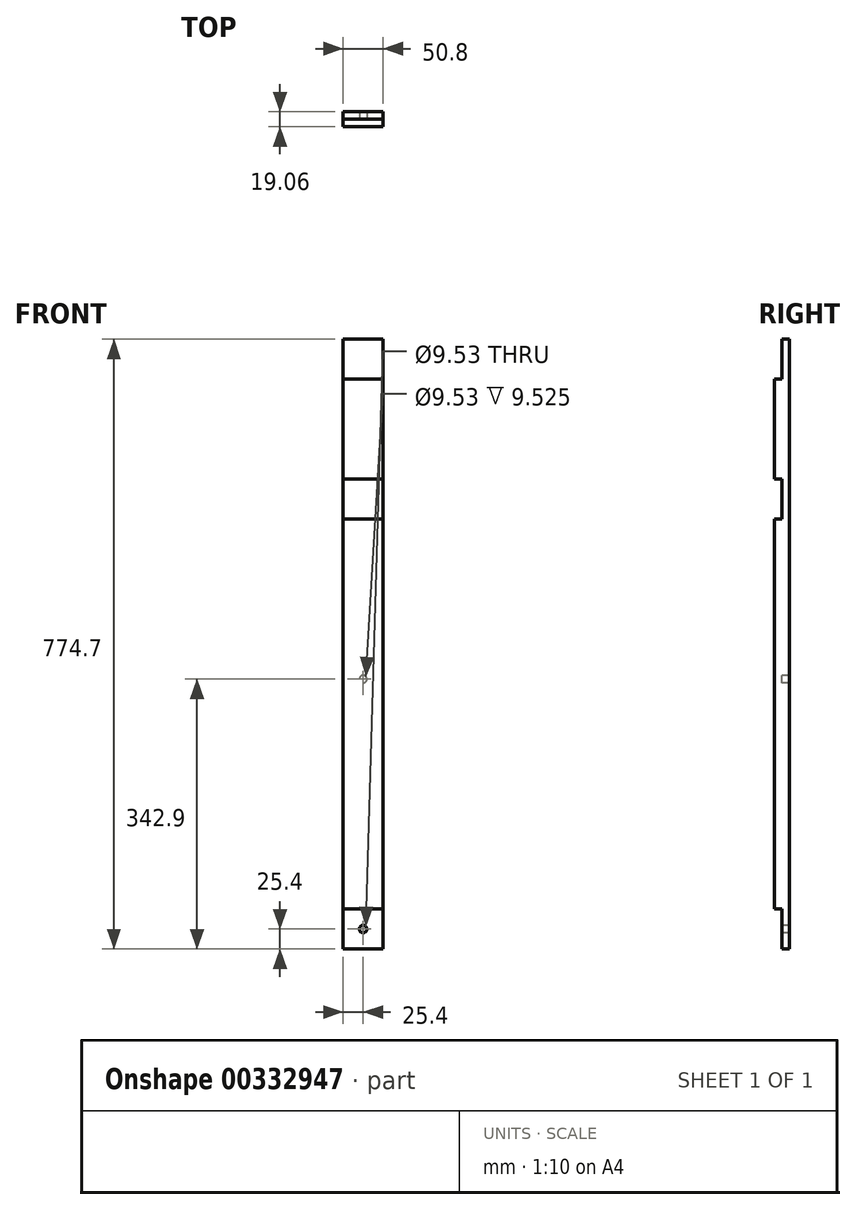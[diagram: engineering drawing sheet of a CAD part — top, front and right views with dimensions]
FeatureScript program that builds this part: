
annotation { "Feature Type Name" : "Feature", "Feature Type Description" : "" }
export const myFeature = defineFeature(function(context is Context, id is Id, definition is map)
    precondition{}
    {
        {
            var Q0;
            Q0=qCreatedBy(makeId("Top.planeOp"),FACE);
            var sketch = newSketch(context, id + "F0", { "sketchPlane" : qUnion([Q0])});
            skLineSegment(sketch, "E0.bottom", {"start": v(25.4, 9.53) * mm, "end": v(-25.4, 9.53) * mm});
            skLineSegment(sketch, "E0.top", {"start": v(25.4, -9.53) * mm, "end": v(-25.4, -9.53) * mm});
            skLineSegment(sketch, "E0.left", {"start": v(25.4, 9.53) * mm, "end": v(25.4, -9.52) * mm});
            skLineSegment(sketch, "E0.right", {"start": v(-25.4, 9.53) * mm, "end": v(-25.4, -9.53) * mm});
            skPoint(sketch, "E0.middle", {"position": v(0, 0) * mm});
            skSolve(sketch);
        }
        {
            var Q0;
            Q0=makeQuery(id+"F0.imprint","IMPRINT",FACE,{"disambiguationData":[TD([[makeQuery(id+"F0.imprint","IMPRINT",EDGE,{"derivedFrom":sQuery(id+"F0.wireOp",EDGE,"E0.bottom")}),1.0]])]});
            var Q1;
            Q1=qSketchRegion(id+"F2",true);
            extrude(context, id + "F1", {"entities" : qUnion([Q0, Q1]), "depth" : 774.7 * mm});
        }
        {
            var Q0;
            Q0=qCreatedBy(makeId("Front.planeOp"),FACE);
            var sketch = newSketch(context, id + "F2", { "sketchPlane" : qUnion([Q0])});
            skLineSegment(sketch, "E1.bottom", {"start": v(-38.77, 0) * mm, "end": v(83.66, 0) * mm});
            skLineSegment(sketch, "E1.top", {"start": v(-38.77, 50.8) * mm, "end": v(83.66, 50.8) * mm});
            skLineSegment(sketch, "E1.left", {"start": v(-38.77, 0) * mm, "end": v(-38.77, 50.8) * mm});
            skLineSegment(sketch, "E1.right", {"start": v(83.66, 0) * mm, "end": v(83.66, 50.8) * mm});
            skLineSegment(sketch, "E2.bottom", {"start": v(-210.36, 723.9) * mm, "end": v(132.8, 723.9) * mm});
            skLineSegment(sketch, "E2.top", {"start": v(-210.36, 774.7) * mm, "end": v(132.8, 774.7) * mm});
            skLineSegment(sketch, "E2.left", {"start": v(-210.36, 723.9) * mm, "end": v(-210.36, 774.7) * mm});
            skLineSegment(sketch, "E2.right", {"start": v(132.8, 723.9) * mm, "end": v(132.8, 774.7) * mm});
            skLineSegment(sketch, "E3.bottom", {"start": v(-168.15, 596.9) * mm, "end": v(92.9, 596.9) * mm});
            skLineSegment(sketch, "E3.top", {"start": v(-168.15, 546.1) * mm, "end": v(92.9, 546.1) * mm});
            skLineSegment(sketch, "E3.left", {"start": v(-168.15, 596.9) * mm, "end": v(-168.15, 546.1) * mm});
            skLineSegment(sketch, "E3.right", {"start": v(92.9, 596.9) * mm, "end": v(92.9, 546.1) * mm});
            skSolve(sketch);
        }
        {
            var Q0;
            Q0=qSketchRegion(id+"F2",true);
            extrude(context, id + "F3", {"entities" : qUnion([Q0]), "operationType" : NewBodyOperationType.REMOVE, "depth" : 25.4 * mm});
        }
        {
            var Q0;
            Q0=qCreatedBy(makeId("Front.planeOp"),FACE);
            var sketch = newSketch(context, id + "F4", { "sketchPlane" : qUnion([Q0])});
            skCircle(sketch, "E4", {"center": v(0, 25.4) * mm, "radius": 4.76 * mm});
            skCircle(sketch, "E5", {"center": v(0, 342.9) * mm, "radius": 4.76 * mm});
            skSolve(sketch);
        }
        {
            var Q0;
            Q0 = qSketchRegion(id + "F4", true);
            extrude(context, id + "F5", {"entities" : qUnion([Q0]), "operationType" : NewBodyOperationType.REMOVE, "oppositeDirection" : true, "depth" : 25.4 * mm});
        }
    });
